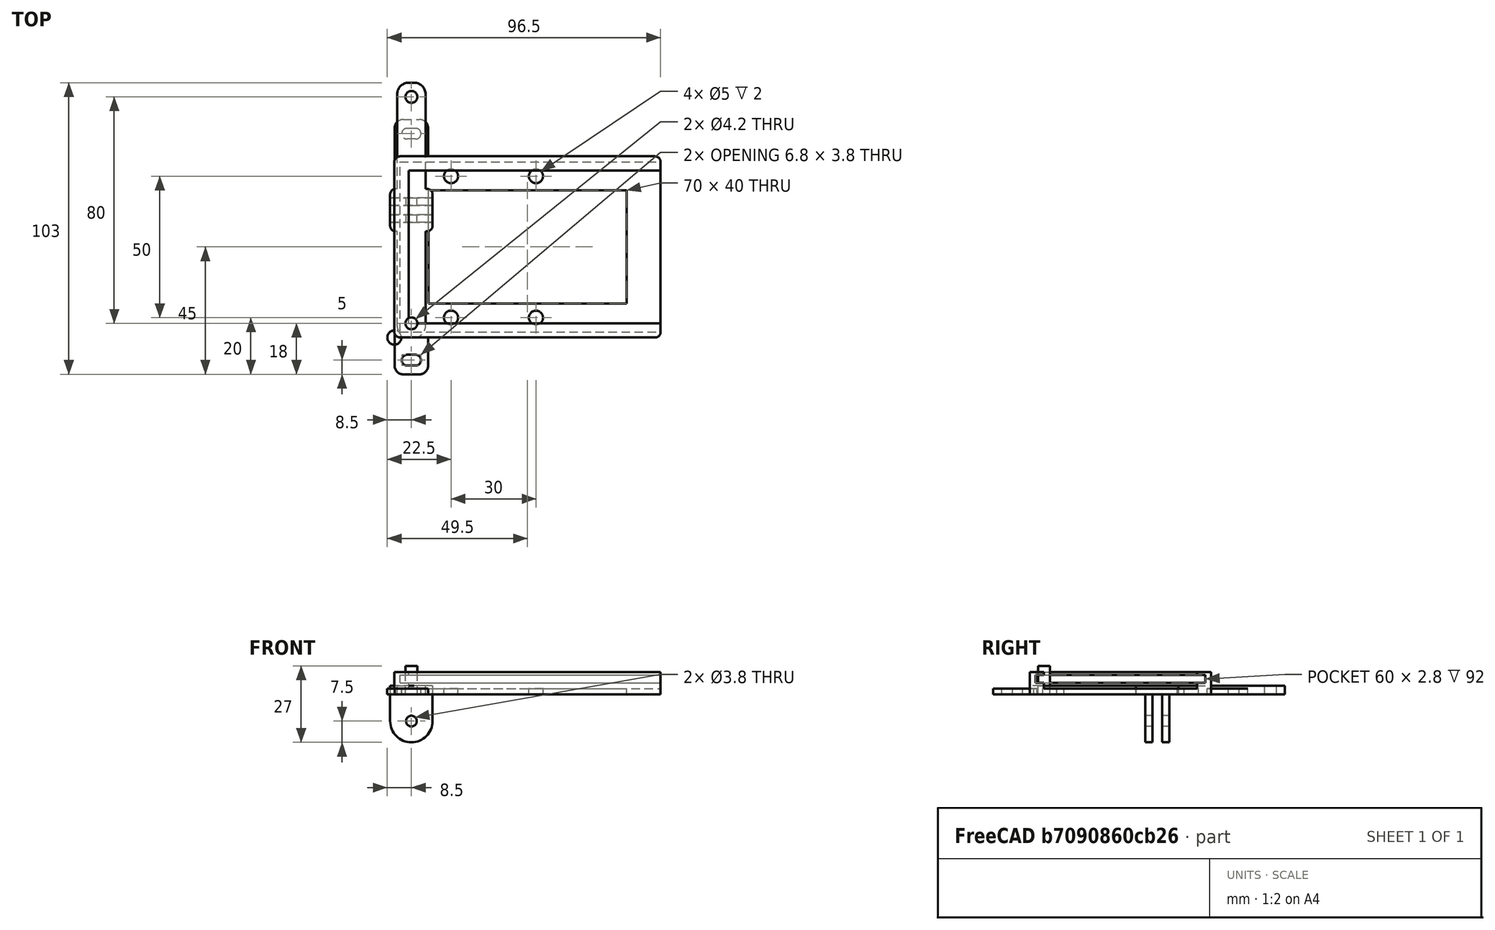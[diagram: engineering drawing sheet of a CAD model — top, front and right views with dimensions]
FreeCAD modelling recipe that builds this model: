
FCSTD DOCUMENT  (FreeCAD 0.19R23578 (Git))
Label: solar_90x60
License: All rights reserved
LicenseURL: http://en.wikipedia.org/wiki/All_rights_reserved
objects: Part::Box×6, Part::Fillet×3, Part::MultiFuse×3, Part::Feature×2, Part::Cylinder×2, Part::FeaturePython×2, Part::Cut×2, Spreadsheet::Sheet×1, App::Part×1
note: 18 computed .brp shape members not serialized (recipe doc carries the construction recipe); baked Part::Feature solids carry a one-line shape summary decoded from their .brp

FEATURE [Part::Box] Box  label="outer cube"
  AttacherType = Attacher::AttachEngine3D
  Height = 7.8
  Length = 94
  Width = 64
  expr: Height = <<p>>.bottom + <<p>>.bottom_space + <<p>>.size_z + <<p>>.top
  expr: Length = <<p>>.size_x + 2 * <<p>>.wall
  expr: Width = <<p>>.size_y + 2 * <<p>>.wall
FEATURE [Spreadsheet::Sheet] Spreadsheet  label="p"
  cells = A1=size_x; B1(size_x)==90mm; A2=size_y; B2(size_y)==60mm; A3=size_z; B3(size_z)==2.8mm; A4=wall; B4(wall)==2mm; A5=bottom_space; B5(bottom_space)==2mm; A6=top; B6(top)==1mm; A7=bottom; B7(bottom)==2mm; A8=pad; B8(pad)==10mm; A9=wire_hole_size; B9(wire_hole_r)==2.5mm; A10=side_lane; B10(side_lane)==3mm
FEATURE [Part::Box] Box001  label="bottom space cube"
  AttacherType = Attacher::AttachEngine3D
  Height = 2
  Length = 89
  Placement = pos=(5,5,2) rot=(0,0,1;0rad)
  Width = 54
  expr: Width = <<p>>.size_y - 2 * <<p>>.side_lane
  expr: Length = <<p>>.size_x - <<p>>.side_lane + <<p>>.wall
  expr: Height = <<p>>.bottom_space
  expr: .Placement.Base.x = <<p>>.wall + <<p>>.side_lane
  expr: .Placement.Base.y = <<p>>.wall + <<p>>.side_lane
  expr: .Placement.Base.z = <<p>>.bottom
FEATURE [Part::Box] Box002  label="panel extract cube"
  AttacherType = Attacher::AttachEngine3D
  Height = 2.8
  Length = 92
  Placement = pos=(2,2,4) rot=(0,0,1;0rad)
  Width = 60
  expr: .Placement.Base.z = <<p>>.bottom + <<p>>.bottom_space
  expr: .Placement.Base.y = <<p>>.wall
  expr: .Placement.Base.x = <<p>>.wall
  expr: Height = <<p>>.size_z
  expr: Length = <<p>>.size_x + <<p>>.wall
  expr: Width = <<p>>.size_y
FEATURE [Part::Box] Box003  label="panel face extract cube"
  AttacherType = Attacher::AttachEngine3D
  Height = 1
  Length = 89
  Placement = pos=(5,5,6.8) rot=(0,0,1;0rad)
  Width = 54
  expr: Width = <<p>>.size_y - 2 * <<p>>.side_lane
  expr: Length = <<p>>.size_x - <<p>>.side_lane + <<p>>.wall
  expr: Height = <<p>>.top
  expr: .Placement.Base.x = <<p>>.wall + <<p>>.side_lane
  expr: .Placement.Base.y = <<p>>.wall + <<p>>.side_lane
  expr: .Placement.Base.z = <<p>>.bottom + <<p>>.bottom_space + <<p>>.size_z
FEATURE [Part::Box] Box004  label="bottom hole cube"
  AttacherType = Attacher::AttachEngine3D
  Height = 2
  Length = 70
  Placement = pos=(12,12,0) rot=(0,0,1;0rad)
  Width = 40
  expr: .Placement.Base.y = <<p>>.wall + <<p>>.pad
  expr: .Placement.Base.x = <<p>>.wall + <<p>>.pad
  expr: Height = <<p>>.bottom
  expr: Length = <<p>>.size_x - 2 * <<p>>.pad
  expr: Width = <<p>>.size_y - 2 * <<p>>.pad
FEATURE [Part::Fillet] Fillet  label="outer fillet"
  Base = -> Box
  Edges = 4 edges r=2: [Edge1,Edge3,Edge5,Edge7]
FEATURE [Part::Feature] Cut002001  label="attach plane y dir001"
  Placement = pos=(0.1,-13,0) rot=(0,0,1;0rad)
  shape: bbox 11.8 x 90 x 2 mm, 20 faces (baked)
FEATURE [Part::MultiFuse] Fusion001  label="body fusion"
  Shapes = -> [Fillet,Cut002001]
FEATURE [Part::Cylinder] Cylinder  label="wire hole"
  Angle = 360
  AttacherType = Attacher::AttachEngine3D
  Height = 2
  Radius = 2.5
  expr: Radius = <<p>>.wire_hole_r
  expr: Height = <<p>>.bottom
FEATURE [Part::FeaturePython] Array  label="wire hole array"  # Draft array (typed FeaturePython)
  Angle = 360
  ArrayType = 0
  Axis = (0,0,1)
  Base = -> Cylinder
  Center = (0,0,0)
  Count = 4
  ExpandArray = false
  Fuse = false
  IntervalAxis = (0,0,0)
  IntervalX = (30,0,0)
  IntervalY = (0,50,0)
  IntervalZ = (0,0,100)
  NumberCircles = 3
  NumberPolar = 5
  NumberX = 2
  NumberY = 2
  NumberZ = 1
  Placement = pos=(20,7,0) rot=(0,0,1;0rad)
  PlacementList = 4 placements: [(0,0,0),(0,50,0),(30,0,0),(30,50,0)]
  RadialDistance = 50
  ScaleList = (4) [(1,1,1),(1,1,1),(1,1,1),(1,1,1)]
  Symmetry = 1
  TangentialDistance = 25
  expr: .IntervalY.y = <<p>>.size_y - 2 * <<p>>.pad + 4 * <<p>>.wire_hole_r
  expr: .Placement.Base.y = <<p>>.wall + <<p>>.pad - 2 * <<p>>.wire_hole_r
FEATURE [Part::MultiFuse] Fusion  label="extract fusion"
  Shapes = -> [Box001,Box002,Box003,Box004,Array]
FEATURE [Part::Cut] Cut  label="body cut"
  Base = -> Fusion001
  Tool = -> Fusion
FEATURE [Part::Feature] Cut001001001  label="side 2"
  Placement = pos=(6,45,3) rot=(0,1,0;3.14159rad)
  shape: bbox 15 x 15 x 20 mm, 16 faces (baked)
FEATURE [Part::Cylinder] Cylinder001  label="insert hole"
  Angle = 360
  AttacherType = Attacher::AttachEngine3D
  Height = 10
  Placement = pos=(6,5,0) rot=(0,0,1;0rad)
  Radius = 2.1
FEATURE [Part::Box] Box005  label="plane cube"
  AttacherType = Attacher::AttachEngine3D
  Height = 3
  Length = 10
  Placement = pos=(1,0,0) rot=(0,0,1;0rad)
  Width = 90
FEATURE [Part::Fillet] Fillet001  label="plane fillet"
  Base = -> Box005
  Edges = 4 edges r=4: [Edge1,Edge3,Edge5,Edge7]
FEATURE [Part::FeaturePython] Array001  label="insert hole array"  # Draft array (typed FeaturePython)
  Angle = 360
  ArrayType = 0
  Axis = (0,0,1)
  Base = -> Cylinder001
  Center = (0,0,0)
  Count = 2
  ExpandArray = false
  Fuse = false
  IntervalAxis = (0,0,0)
  IntervalX = (100,0,0)
  IntervalY = (0,80,0)
  IntervalZ = (0,0,100)
  NumberCircles = 3
  NumberPolar = 5
  NumberX = 1
  NumberY = 2
  NumberZ = 1
  PlacementList = 2 placements: [(6,5,0),(6,85,0)]
  RadialDistance = 50
  ScaleList = (2) [(1,1,1),(1,1,1)]
  Symmetry = 1
  TangentialDistance = 25
FEATURE [Part::Fillet] Fillet002  label="side 2 fillet"
  Base = -> Cut001001001
  Edges = 4 edges r=2: [Edge1,Edge11,Edge13,Edge42]
FEATURE [Part::MultiFuse] Fusion002  label="attachment fusion"
  Shapes = -> [Fillet001,Fillet002]
FEATURE [Part::Cut] Cut001001002  label="attachment cut"
  Base = -> Fusion002
  Tool = -> Array001
FEATURE [App::Part] Part001  label="attachment part"
  Group = -> [Cut001001002]
  Origin = -> Origin001
  Placement = pos=(0,-13,0) rot=(0,0,1;0rad)
